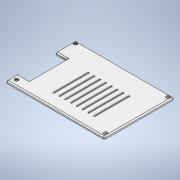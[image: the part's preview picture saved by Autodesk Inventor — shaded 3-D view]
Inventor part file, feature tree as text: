
AUTODESK INVENTOR PART (.ipt)
format: ipt  version: 2022 (Build 260153000, 153)  size: 225,280 bytes
history: native  units: mm
features: extrude x5, sketch x4, fillet x3, pattern_linear x1
ambient origin geometry x8: Origin, YZ Plane, XZ Plane, XY Plane, X Axis, Y Axis, Z Axis, Center Point
bodies: Solid1 (feature_tree)
feature tree (13):
  sketch  "Sketch1"  dims[d4=4.0mm d5=0.0mm d6=30.0mm d7=0.0mm]
  extrude  "Extrusion1"  Depth=30.0mm TaperAngle=0.0deg
  extrude  "Extrusion2"  TaperAngle=0.0deg  [1 undecoded]
  fillet  "Fillet1"  [1 undecoded]
  extrude  "Extrusion3"  Depth=10.0mm
  extrude  "Extrusion4"  Depth=2.0mm
  pattern_linear  "Rectangular Pattern1"  Spacing1=0.75mm  [1 undecoded]
  extrude  "Extrusion5"  Depth=2.0mm TaperAngle=0.0deg
  fillet  "Fillet2"  Radius=2.0mm
  fillet  "Fillet3"  Radius=2.0mm
  sketch  "Sketch2"  dims[d8=1.0mm d9=0.0mm d10=0.0mm d11=0.0mm d12=0.0mm]
  sketch  "Sketch3"  dims[d13=80.0mm d15=10.0mm d16=0.75mm]
  sketch  "Sketch4"  dims[d17=0.75mm d18=0.75mm d19=0.75mm d20=1.5mm d21=0.0mm d22=2.0mm d23=2.0mm d0=0.5mm d1=0.872665mm d2=0.5mm d3=0.872665mm d14=0.0mm d24=0.0mm d25=0.0mm]
note: 3 required parameter values undecoded (feature->parameter linkage not recoverable at this tier; creation-order binding heuristic only, values carry confidence <= 0.55)
